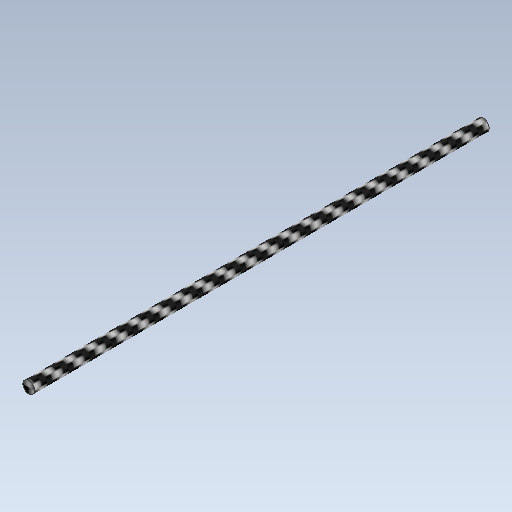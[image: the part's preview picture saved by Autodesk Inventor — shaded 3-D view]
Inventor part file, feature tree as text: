
AUTODESK INVENTOR PART (.ipt)
format: ipt  version: 2020 (Build 240168000, 168)  size: 104,448 bytes
history: native  units: in
note: dims shown in document units (in); Inventor stores cm internally (conversion verified against a paired STEP export)
features: extrude x1, sketch x1
ambient origin geometry x8: Origin, YZ Plane, XZ Plane, XY Plane, X Axis, Y Axis, Z Axis, Center Point
bodies: Solid1 (feature_tree)
feature tree (2):
  extrude  "Extrusion1"  Depth=3.1106in
  sketch  "Sketch1"  dims[d0=0.0827in d1=3.1106in d2=0.0in]
